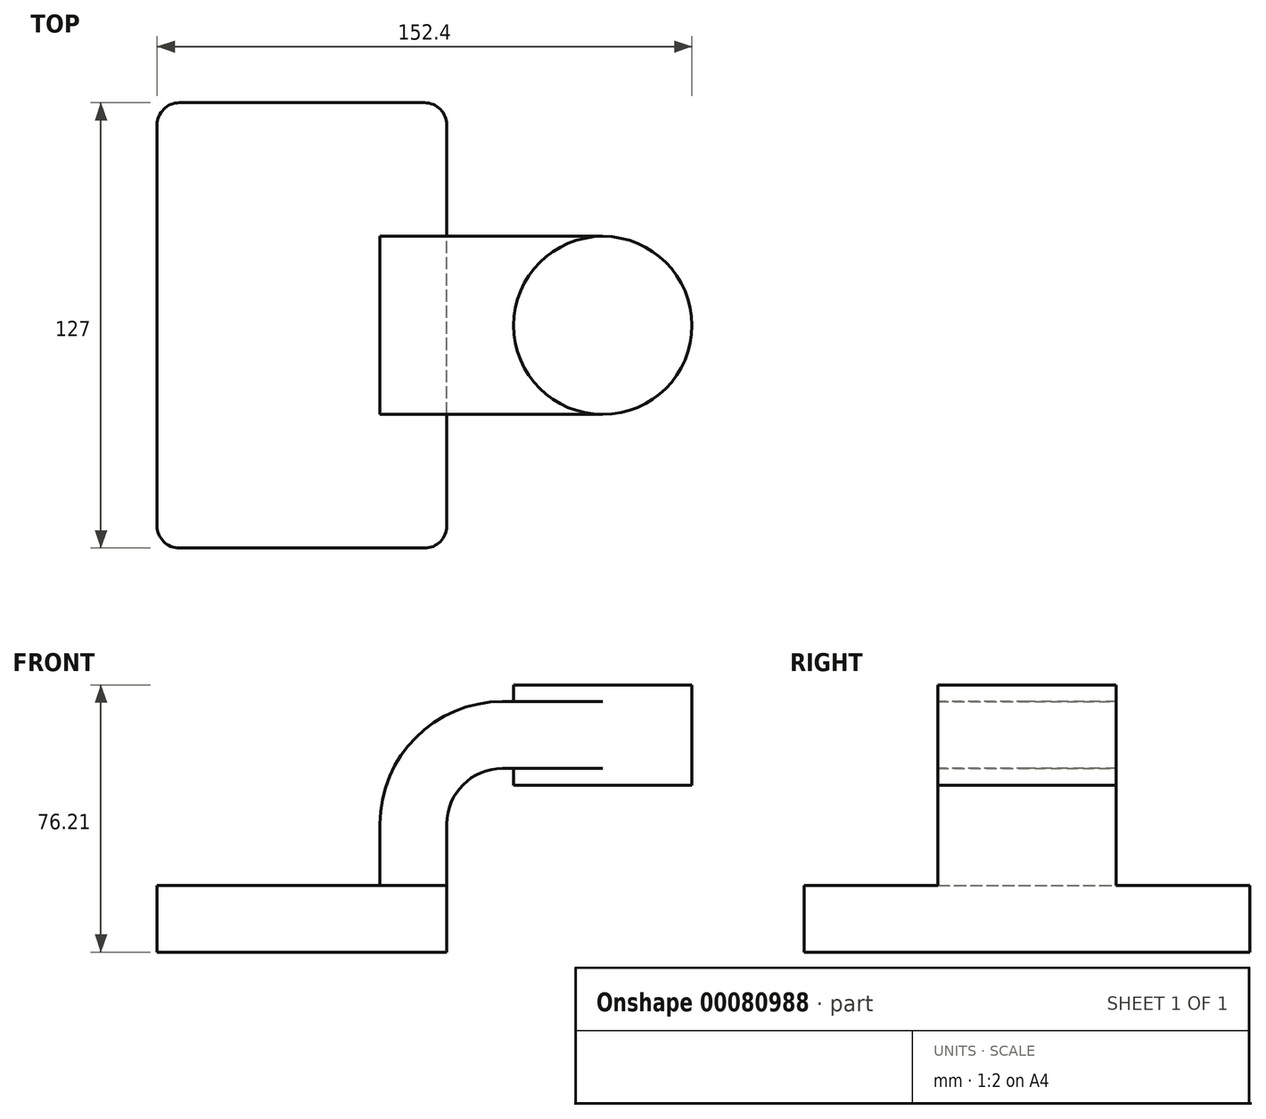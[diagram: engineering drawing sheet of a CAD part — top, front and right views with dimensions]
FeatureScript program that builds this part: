
annotation { "Feature Type Name" : "Feature", "Feature Type Description" : "" }
export const myFeature = defineFeature(function(context is Context, id is Id, definition is map)
    precondition{}
    {
        {
            var Q0;
            Q0=qCreatedBy(makeId("Front.planeOp"),FACE);
            var sketch = newSketch(context, id + "F0", { "sketchPlane" : qUnion([Q0])});
            skLineSegment(sketch, "E0.left", {"start": v(0, 0) * mm, "end": v(0, 0) * mm});
            skLineSegment(sketch, "E1.bottom", {"start": v(41.27, 9.53) * mm, "end": v(-41.27, 9.53) * mm});
            skLineSegment(sketch, "E1.top", {"start": v(41.28, -9.52) * mm, "end": v(-41.27, -9.52) * mm});
            skLineSegment(sketch, "E1.left", {"start": v(41.28, 9.53) * mm, "end": v(41.28, -9.52) * mm});
            skLineSegment(sketch, "E1.right", {"start": v(-41.27, 9.53) * mm, "end": v(-41.27, -9.52) * mm});
            skPoint(sketch, "E1.middle", {"position": v(0, 0) * mm});
            skLineSegment(sketch, "E2.bottom", {"start": v(111.13, 66.68) * mm, "end": v(60.33, 66.68) * mm});
            skLineSegment(sketch, "E2.top", {"start": v(111.13, 38.1) * mm, "end": v(60.33, 38.1) * mm});
            skLineSegment(sketch, "E2.left", {"start": v(111.13, 66.68) * mm, "end": v(111.13, 38.1) * mm});
            skLineSegment(sketch, "E2.right", {"start": v(60.33, 66.68) * mm, "end": v(60.33, 38.1) * mm});
            skPoint(sketch, "E2.middle", {"position": v(85.73, 52.39) * mm});
            skLineSegment(sketch, "E3", {"start": v(41.27, 9.53) * mm, "end": v(41.27, 26.99) * mm});
            skArc(sketch, "E4", {"start": v(41.27, 26.99) * mm, "mid": v(45.92, 38.21) * mm, "end": v(57.15, 42.86) * mm});
            skLineSegment(sketch, "E5", {"start": v(57.15, 42.86) * mm, "end": v(85.73, 42.86) * mm});
            skLineSegment(sketch, "E6.0", {"start": v(57.15, 61.91) * mm, "end": v(85.73, 61.91) * mm});
            skArc(sketch, "E6.1", {"start": v(22.22, 26.99) * mm, "mid": v(32.45, 51.68) * mm, "end": v(57.15, 61.91) * mm});
            skLineSegment(sketch, "E6.2", {"start": v(22.22, 9.53) * mm, "end": v(22.22, 26.99) * mm});
            skLineSegment(sketch, "E7", {"start": v(85.73, 38.1) * mm, "end": v(85.73, 66.68) * mm});
            skFitSpline(sketch, "E8", {"points": [v(-41.27, 9.52) * mm, v(57.15, 61.91) * mm], "startDerivative": vector(0, 70.77) * mm, "endDerivative": vector(125.06, 0) * mm});
            skSolve(sketch);
        }
        {
            var Q0;
            Q0=makeQuery(id+"F0.imprint","IMPRINT",FACE,{"disambiguationData":[TD([[makeQuery(id+"F0.imprint","IMPRINT",EDGE,{"derivedFrom":sQuery(id+"F0.wireOp",EDGE,"E1.top")}),-1.0]])]});
            extrude(context, id + "F1", {"entities" : qUnion([Q0]), "endBound" : BoundingType.SYMMETRIC, "depth" : 127 * mm});
        }
        {
            var Q0;
            {var subQ1=sQuery(id+"F0.wireOp",EDGE,"E3");Q0=makeQuery(id+"F0.imprint","IMPRINT",FACE,{"disambiguationData":[TD([[makeQuery(id+"F0.imprint","IMPRINT",EDGE,{"derivedFrom":subQ1}),1.0]])]});}
            var Q1;
            {var subQ0=sQuery(id+"F0.wireOp",EDGE,"E6.0");var subQ1=sQuery(id+"F0.wireOp",EDGE,"E2.right");var subQ2=makeQuery(id+"F0.imprint","INTERSECT",VERTEX,{"derivedFrom":[subQ1,subQ0]});Q1=makeQuery(id+"F0.imprint","IMPRINT",FACE,{"disambiguationData":[TD([[makeQuery(id+"F0.imprint","IMPRINT",EDGE,{"disambiguationData":[TD([[subQ2,-1.0]])],"derivedFrom":subQ1}),1.0]])]});}
            extrude(context, id + "F2", {"entities" : qUnion([Q0, Q1]), "operationType" : NewBodyOperationType.ADD, "endBound" : BoundingType.SYMMETRIC, "depth" : 50.8 * mm});
        }
        {
            var Q0;
            {var subQ0=sQuery(id+"F0.wireOp",EDGE,"E2.left");Q0=makeQuery(id+"F0.imprint","IMPRINT",FACE,{"disambiguationData":[TD([[makeQuery(id+"F0.imprint","IMPRINT",EDGE,{"derivedFrom":subQ0}),-1.0]])]});}
            var Q1;
            Q1=sQuery(id+"F0.wireOp",EDGE,"E7");
            revolve(context, id + "F3", {"operationType" : NewBodyOperationType.ADD, "entities" : qUnion([Q0]), "axis" : qUnion([Q1]), "revolveType" : RevolveType.FULL});
        }
        {
            var Q0;
            Q0=makeQuery(id+"F0.imprint","IMPRINT",FACE,{"disambiguationData":[TD([[makeQuery(id+"F0.imprint","IMPRINT",EDGE,{"derivedFrom":sQuery(id+"F0.wireOp",EDGE,"E6.1")}),1.0]])]});
            extrude(context, id + "F4", {"entities" : qUnion([Q0]), "operationType" : NewBodyOperationType.ADD, "endBound" : BoundingType.SYMMETRIC, "depth" : 15.88 * mm});
        }
        {
            var Q0;
            Q0=makeQuery(id+"F1.opExtrude","CAP_EDGE",EDGE,{"disambiguationData":[OSD([sQuery(id+"F0.wireOp",EDGE,"E1.right")])],"isStart":false});
            var Q1;
            Q1=makeQuery(id+"F1.opExtrude","CAP_EDGE",EDGE,{"disambiguationData":[OSD([sQuery(id+"F0.wireOp",EDGE,"E1.left")])],"isStart":false});
            var Q2;
            Q2=makeQuery(id+"F1.opExtrude","CAP_EDGE",EDGE,{"disambiguationData":[OSD([sQuery(id+"F0.wireOp",EDGE,"E1.right")])],"isStart":true});
            var Q3;
            Q3=makeQuery(id+"F1.opExtrude","CAP_EDGE",EDGE,{"disambiguationData":[OSD([sQuery(id+"F0.wireOp",EDGE,"E1.left")])],"isStart":true});
            fillet(context, id + "F5", {"entities" : qUnion([Q0, Q1, Q2, Q3]), "radius" : 6.35 * mm, "tangentPropagation" : true, "allowEdgeOverflow" : false});
        }
    });
